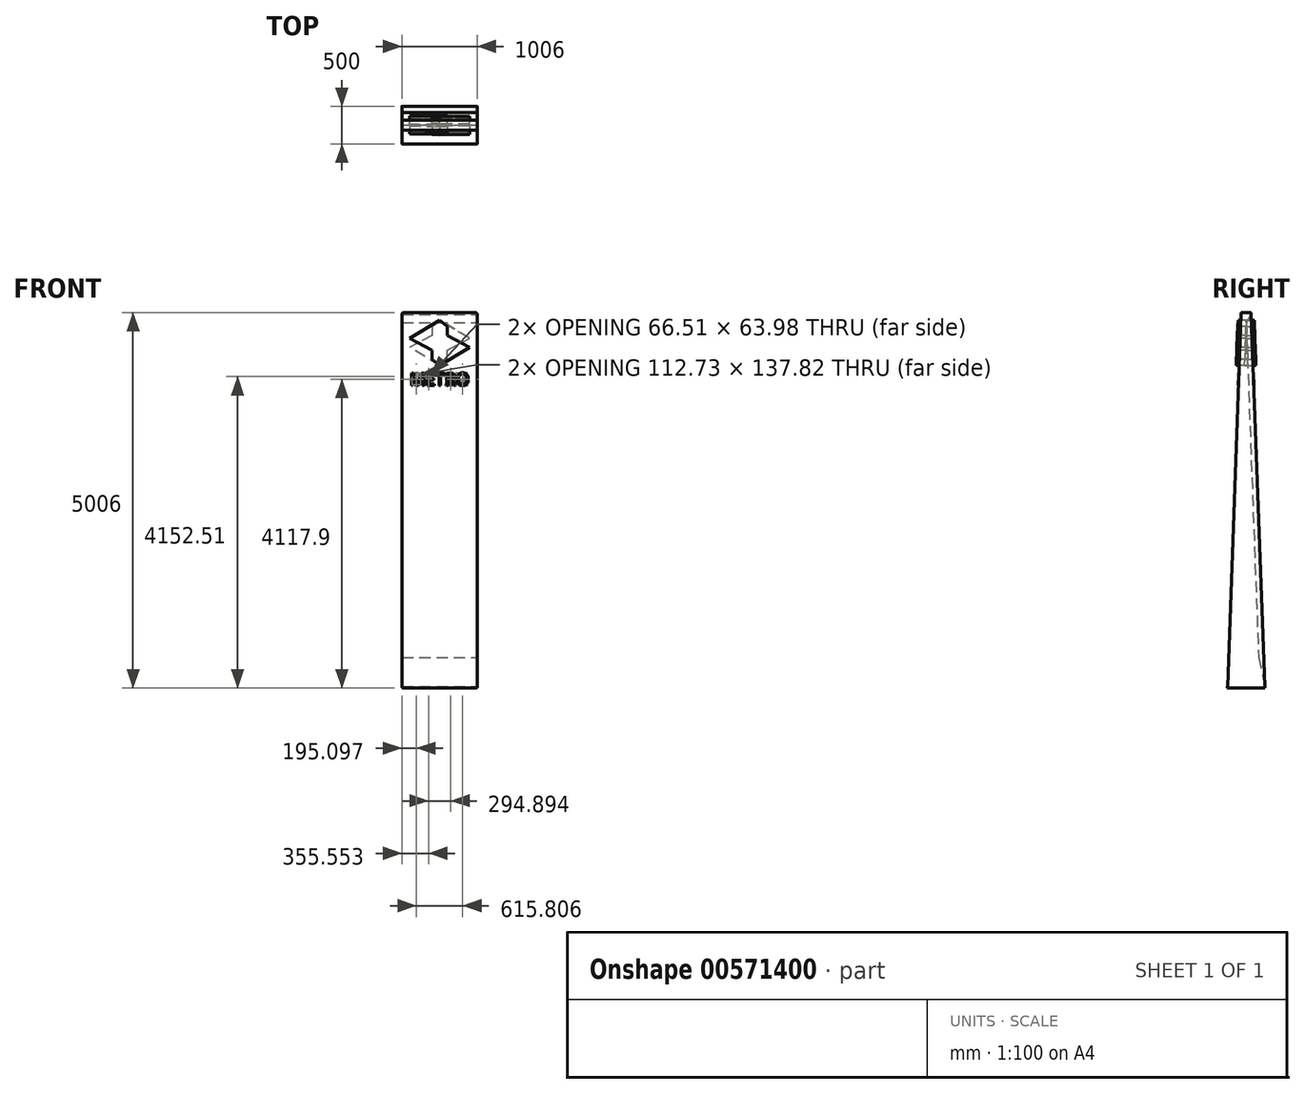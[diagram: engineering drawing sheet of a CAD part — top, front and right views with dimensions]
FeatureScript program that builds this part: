
annotation { "Feature Type Name" : "Feature", "Feature Type Description" : "" }
export const myFeature = defineFeature(function(context is Context, id is Id, definition is map)
    precondition{}
    {
        {
            var Q0;
            Q0=qCreatedBy(makeId("Front.planeOp"),FACE);
            var sketch = newSketch(context, id + "F0", { "sketchPlane" : qUnion([Q0])});
            skLineSegment(sketch, "E0.bottom", {"start": v(-500, 2500) * mm, "end": v(500, 2500) * mm});
            skLineSegment(sketch, "E0.top", {"start": v(-500, -2500) * mm, "end": v(500, -2500) * mm});
            skLineSegment(sketch, "E0.left", {"start": v(-500, 2500) * mm, "end": v(-500, -2500) * mm});
            skLineSegment(sketch, "E0.right", {"start": v(500, 2500) * mm, "end": v(500, -2500) * mm});
            skSolve(sketch);
        }
        {
            var Q0;
            Q0=qSketchRegion(id+"F0",true);
            extrude(context, id + "F1", {"entities" : qUnion([Q0]), "depth" : 500 * mm, "offsetDistance" : 25 * mm, "symmetric" : true});
        }
        {
            var Q0;
            Q0=makeQuery(id+"F1.opExtrude","SWEPT_FACE",FACE,{"disambiguationData":[OSD([sQuery(id+"F0.wireOp",EDGE,"E0.right")])]});
            var sketch = newSketch(context, id + "F2", { "sketchPlane" : qUnion([Q0])});
            skLineSegment(sketch, "E1", {"start": v(0, -2500) * mm, "end": v(0, 2500) * mm, "construction": true});
            skLineSegment(sketch, "E2", {"start": v(-250, -2500) * mm, "end": v(-62.78, 2560) * mm});
            skLineSegment(sketch, "E3", {"start": v(-250, 2500) * mm, "end": v(-250, -2500) * mm});
            skLineSegment(sketch, "E4.MirrorCS", {"start": v(250, 2500) * mm, "end": v(250, -2500) * mm});
            skLineSegment(sketch, "E5.MirrorCS", {"start": v(250, -2500) * mm, "end": v(62.78, 2560) * mm});
            skLineSegment(sketch, "E6", {"start": v(250, 2500) * mm, "end": v(250, 2560) * mm});
            skLineSegment(sketch, "E7", {"start": v(250, 2560) * mm, "end": v(62.78, 2560) * mm});
            skLineSegment(sketch, "E8", {"start": v(-62.78, 2560) * mm, "end": v(-250, 2560) * mm});
            skLineSegment(sketch, "E9", {"start": v(-250, 2560) * mm, "end": v(-250, 2500) * mm});
            skPoint(sketch, "E10", {"position": v(65, 2500) * mm});
            skSolve(sketch);
        }
        {
            var Q0;
            Q0 = qSketchRegion(id + "F2", true);
            extrude(context, id + "F3", {"entities" : qUnion([Q0]), "operationType" : NewBodyOperationType.REMOVE, "endBound" : BoundingType.THROUGH_ALL, "oppositeDirection" : true, "depth" : 25 * mm, "offsetDistance" : 25 * mm});
        }
        {
            var Q0;
            Q0=makeQuery(id+"F1.opExtrude","SWEPT_EDGE",EDGE,{"disambiguationData":[OSD([sQuery(id+"F0.wireOp",EDGE,"E0.bottom"),sQuery(id+"F0.wireOp",EDGE,"E0.left")])]});
            var Q1;
            Q1=makeQuery(id+"F1.opExtrude","SWEPT_EDGE",EDGE,{"disambiguationData":[OSD([sQuery(id+"F0.wireOp",EDGE,"E0.bottom"),sQuery(id+"F0.wireOp",EDGE,"E0.right")])]});
            var Q2;
            Q2=makeQuery(id+"F1.opExtrude","SWEPT_EDGE",EDGE,{"disambiguationData":[OSD([sQuery(id+"F0.wireOp",EDGE,"E0.top"),sQuery(id+"F0.wireOp",EDGE,"E0.left")])]});
            var Q3;
            Q3=makeQuery(id+"F1.opExtrude","SWEPT_EDGE",EDGE,{"disambiguationData":[OSD([sQuery(id+"F0.wireOp",EDGE,"E0.top"),sQuery(id+"F0.wireOp",EDGE,"E0.right")])]});
            fillet(context, id + "F4", {"entities" : qUnion([Q0, Q1, Q2, Q3]), "radius" : 20 * mm, "tangentPropagation" : true, "allowEdgeOverflow" : false});
        }
        {
            var Q0;
            Q0=qCreatedBy(makeId("Front.planeOp"),FACE);
            var sketch = newSketch(context, id + "F5", { "sketchPlane" : qUnion([Q0])});
            skLineSegment(sketch, "E11.0.0", {"start": v(480, -2500) * mm, "end": v(-480, -2500) * mm});
            skArc(sketch, "E11.0.1", {"start": v(-480, -2500) * mm, "mid": v(-494.14, -2494.14) * mm, "end": v(-500, -2480) * mm});
            skLineSegment(sketch, "E11.0.2", {"start": v(-500, -2480) * mm, "end": v(-500, 2480) * mm});
            skArc(sketch, "E11.0.3", {"start": v(-500, 2480) * mm, "mid": v(-494.14, 2494.14) * mm, "end": v(-480, 2500) * mm});
            skLineSegment(sketch, "E11.0.4", {"start": v(-480, 2500) * mm, "end": v(480, 2500) * mm});
            skArc(sketch, "E11.0.5", {"start": v(480, 2500) * mm, "mid": v(494.14, 2494.14) * mm, "end": v(500, 2480) * mm});
            skLineSegment(sketch, "E11.0.6", {"start": v(500, 2480) * mm, "end": v(500, -2480) * mm});
            skArc(sketch, "E11.0.7", {"start": v(500, -2480) * mm, "mid": v(494.14, -2494.14) * mm, "end": v(480, -2500) * mm});
            skArc(sketch, "E12.0", {"start": v(-503, 2480) * mm, "mid": v(-496.26, 2496.26) * mm, "end": v(-480, 2503) * mm});
            skLineSegment(sketch, "E12.1", {"start": v(-503, -2480) * mm, "end": v(-503, 2480) * mm});
            skLineSegment(sketch, "E12.2", {"start": v(-480, 2503) * mm, "end": v(480, 2503) * mm});
            skArc(sketch, "E12.3", {"start": v(-480, -2503) * mm, "mid": v(-496.26, -2496.26) * mm, "end": v(-503, -2480) * mm});
            skArc(sketch, "E12.4", {"start": v(480, 2503) * mm, "mid": v(496.26, 2496.26) * mm, "end": v(503, 2480) * mm});
            skLineSegment(sketch, "E12.5", {"start": v(503, 2480) * mm, "end": v(503, -2480) * mm});
            skArc(sketch, "E12.6", {"start": v(503, -2480) * mm, "mid": v(496.26, -2496.26) * mm, "end": v(480, -2503) * mm});
            skLineSegment(sketch, "E12.7", {"start": v(480, -2503) * mm, "end": v(-480, -2503) * mm});
            skSolve(sketch);
        }
        {
            var Q0;
            Q0=qSketchRegion(id+"F5",true);
            extrude(context, id + "F6", {"entities" : qUnion([Q0]), "depth" : 500 * mm, "offsetDistance" : 25 * mm, "symmetric" : true});
        }
        {
            var Q0;
            Q0=qCreatedBy(makeId("Front.planeOp"),FACE);
            cPlane(context, id + "F7", {"entities" : qUnion([Q0]), "cplaneType" : CPlaneType.OFFSET, "offset" : 730 * mm, "width" : 150 * mm, "height" : 150 * mm});
        }
        {
            var Q0;
            Q0 = qSketchRegion(id + "F2", true);
            extrude(context, id + "F8", {"entities" : qUnion([Q0]), "operationType" : NewBodyOperationType.REMOVE, "oppositeDirection" : true, "depth" : 5000 * mm, "offsetDistance" : 25 * mm, "symmetric" : true});
        }
        {
            var Q0;
            Q0=qCreatedBy(id+"F7.planeOp",FACE);
            var sketch = newSketch(context, id + "F9", { "sketchPlane" : qUnion([Q0])});
            skLineSegment(sketch, "E13", {"start": v(0, 0) * mm, "end": v(0, 2768.76) * mm, "construction": true});
            skLineSegment(sketch, "E14.0", {"start": v(-479.83, 2500) * mm, "end": v(480, 2500) * mm, "construction": true});
            skLineSegment(sketch, "E15", {"start": v(-400, 2100) * mm, "end": v(400, 2100) * mm, "construction": true});
            skLineSegment(sketch, "E16", {"start": v(-400, 2400) * mm, "end": v(-400, 1800) * mm, "construction": true});
            skLineSegment(sketch, "E17", {"start": v(-400, 2400) * mm, "end": v(400, 2400) * mm, "construction": true});
            skLineSegment(sketch, "E18", {"start": v(400, 2400) * mm, "end": v(400, 1800) * mm, "construction": true});
            skLineSegment(sketch, "E19", {"start": v(400, 1800) * mm, "end": v(-400, 1800) * mm, "construction": true});
            skLineSegment(sketch, "E20", {"start": v(-120, 1800) * mm, "end": v(-120, 2400) * mm, "construction": true});
            skLineSegment(sketch, "E21", {"start": v(120, 2400) * mm, "end": v(120, 1800) * mm, "construction": true});
            skLineSegment(sketch, "E22", {"start": v(-400, 2160) * mm, "end": v(400, 2160) * mm, "construction": true});
            skLineSegment(sketch, "E23", {"start": v(-400, 2040) * mm, "end": v(400, 2040) * mm, "construction": true});
            skPoint(sketch, "E24", {"position": v(0, 2400) * mm});
            skLineSegment(sketch, "E25", {"start": v(100, 2320) * mm, "end": v(100, 2200) * mm});
            skLineSegment(sketch, "E26", {"start": v(100, 2200) * mm, "end": v(400, 2040) * mm});
            skLineSegment(sketch, "E27", {"start": v(-100, 1880) * mm, "end": v(-100, 2000) * mm});
            skLineSegment(sketch, "E28", {"start": v(-100, 2000) * mm, "end": v(-400, 2160) * mm});
            skLineSegment(sketch, "E29", {"start": v(-100, 1880) * mm, "end": v(0, 1800) * mm});
            skLineSegment(sketch, "E30", {"start": v(0, 1800) * mm, "end": v(400, 2040) * mm});
            skLineSegment(sketch, "E31", {"start": v(100, 2320) * mm, "end": v(0, 2400) * mm});
            skLineSegment(sketch, "E32", {"start": v(-400, 2160) * mm, "end": v(0, 2400) * mm});
            skSolve(sketch);
        }
        {
            var Q0;
            Q0=qSketchRegion(id+"F9",true);
            extrude(context, id + "F10", {"entities" : qUnion([Q0]), "oppositeDirection" : true, "depth" : 800 * mm, "offsetDistance" : 25 * mm});
        }
        {
            var Q0;
            Q0=makeQuery(id+"F1.opExtrude","SWEPT_FACE",FACE,{"disambiguationData":[OSD([sQuery(id+"F0.wireOp",EDGE,"E0.right")])]});
            var sketch = newSketch(context, id + "F11", { "sketchPlane" : qUnion([Q0])});
            skLineSegment(sketch, "E33.0", {"start": v(-289.57, -2487.76) * mm, "end": v(-106.05, 2472.24) * mm});
            skLineSegment(sketch, "E34", {"start": v(-106.05, 2472.24) * mm, "end": v(-840.5, 2445.07) * mm});
            skLineSegment(sketch, "E35", {"start": v(-840.5, 2445.07) * mm, "end": v(-289.57, -2487.76) * mm});
            skLineSegment(sketch, "E36", {"start": v(65.74, 2480) * mm, "end": v(918.94, 2448.43) * mm});
            skLineSegment(sketch, "E37", {"start": v(918.94, 2448.43) * mm, "end": v(249.26, -2480) * mm});
            skLineSegment(sketch, "E38", {"start": v(65.74, 2480) * mm, "end": v(0, 2371.47) * mm});
            skPoint(sketch, "E38.endSnap0", {"position": v(0, 2480) * mm});
            skLineSegment(sketch, "E39", {"start": v(0, 2371.47) * mm, "end": v(165.33, -2096.89) * mm});
            skLineSegment(sketch, "E40", {"start": v(165.33, -2096.89) * mm, "end": v(249.26, -2480) * mm});
            skSolve(sketch);
        }
        {
            var Q0;
            Q0 = qSketchRegion(id + "F11", true);
            extrude(context, id + "F12", {"entities" : qUnion([Q0]), "operationType" : NewBodyOperationType.REMOVE, "endBound" : BoundingType.THROUGH_ALL, "oppositeDirection" : true, "depth" : 25 * mm, "offsetDistance" : 25 * mm});
        }
        {
            var Q0;
            Q0=qCreatedBy(id+"F7.planeOp",FACE);
            var sketch = newSketch(context, id + "F13", { "sketchPlane" : qUnion([Q0])});
            skText(sketch, "E41", { "text": "METRO", "fontName": "OpenSans-Regular.ttf"});
            const initialGuessF13  = {"E41": [-0.39992, 1.53123, 1, 0, 0.16877]};
            skSetInitialGuess(sketch, initialGuessF13);
            skSolve(sketch);
        }
        {
            var Q0;
            Q0=qSketchRegion(id+"F13",true);
            var Q1;
            Q1=makeQuery(id+"F3.boolean.opBoolean","COPY",FACE,{"derivedFrom":makeQuery(id+"F3.opExtrude","SWEPT_FACE",FACE,{"disambiguationData":[OSD([sQuery(id+"F2.wireOp",EDGE,"E2")])]})});
            extrude(context, id + "F14", {"entities" : qUnion([Q0]), "endBound" : BoundingType.UP_TO_SURFACE, "oppositeDirection" : true, "depth" : 25 * mm, "endBoundEntityFace" : qUnion([Q1]), "offsetDistance" : 25 * mm});
        }
        {
            var Q0;
            Q0=makeQuery(id+"F1.opExtrude","SWEPT_FACE",FACE,{"disambiguationData":[OSD([sQuery(id+"F0.wireOp",EDGE,"E0.right")])]});
            var sketch = newSketch(context, id + "F15", { "sketchPlane" : qUnion([Q0])});
            skLineSegment(sketch, "E42.0", {"start": v(-109.8, 1424.3) * mm, "end": v(-98.9, 1718.76) * mm});
            skLineSegment(sketch, "E43", {"start": v(-98.9, 1718.76) * mm, "end": v(-869.9, 1736.78) * mm});
            skLineSegment(sketch, "E44", {"start": v(-869.9, 1736.78) * mm, "end": v(-869.9, 1424.3) * mm});
            skLineSegment(sketch, "E45", {"start": v(-869.9, 1424.3) * mm, "end": v(-109.8, 1424.3) * mm});
            skSolve(sketch);
        }
        {
            var Q0;
            Q0=qSketchRegion(id+"F15",true);
            extrude(context, id + "F16", {"entities" : qUnion([Q0]), "operationType" : NewBodyOperationType.REMOVE, "endBound" : BoundingType.THROUGH_ALL, "oppositeDirection" : true, "depth" : 25 * mm, "offsetDistance" : 25 * mm});
        }
        {
            var Q0;
            Q0=makeQuery(id+"F10.opExtrude","SWEPT_BODY",BODY,{"disambiguationData":[OSD([sQuery(id+"F9.wireOp",EDGE,"E25"),sQuery(id+"F9.wireOp",EDGE,"E26"),sQuery(id+"F9.wireOp",EDGE,"E27"),sQuery(id+"F9.wireOp",EDGE,"E28"),sQuery(id+"F9.wireOp",EDGE,"E29"),sQuery(id+"F9.wireOp",EDGE,"E30"),sQuery(id+"F9.wireOp",EDGE,"E31"),sQuery(id+"F9.wireOp",EDGE,"E32")])]});
            var Q1;
            Q1=makeQuery(id+"F14.opExtrude","SWEPT_BODY",BODY,{"disambiguationData":[OSD([sQuery(id+"F13.wireOp",EDGE,"E41.sketch_text.stroke-56"),sQuery(id+"F13.wireOp",EDGE,"E41.sketch_text.stroke-57"),sQuery(id+"F13.wireOp",EDGE,"E41.sketch_text.stroke-58"),sQuery(id+"F13.wireOp",EDGE,"E41.sketch_text.stroke-59"),sQuery(id+"F13.wireOp",EDGE,"E41.sketch_text.stroke-60"),sQuery(id+"F13.wireOp",EDGE,"E41.sketch_text.stroke-61"),sQuery(id+"F13.wireOp",EDGE,"E41.sketch_text.stroke-62"),sQuery(id+"F13.wireOp",EDGE,"E41.sketch_text.stroke-63"),sQuery(id+"F13.wireOp",EDGE,"E41.sketch_text.stroke-64"),sQuery(id+"F13.wireOp",EDGE,"E41.sketch_text.stroke-65"),sQuery(id+"F13.wireOp",EDGE,"E41.sketch_text.stroke-66"),sQuery(id+"F13.wireOp",EDGE,"E41.sketch_text.stroke-67"),sQuery(id+"F13.wireOp",EDGE,"E41.sketch_text.stroke-68"),sQuery(id+"F13.wireOp",EDGE,"E41.sketch_text.stroke-69"),sQuery(id+"F13.wireOp",EDGE,"E41.sketch_text.stroke-70"),sQuery(id+"F13.wireOp",EDGE,"E41.sketch_text.stroke-71")])]});
            var Q2;
            Q2=makeQuery(id+"F14.opExtrude","SWEPT_BODY",BODY,{"disambiguationData":[OSD([sQuery(id+"F13.wireOp",EDGE,"E41.sketch_text.stroke-38"),sQuery(id+"F13.wireOp",EDGE,"E41.sketch_text.stroke-39"),sQuery(id+"F13.wireOp",EDGE,"E41.sketch_text.stroke-40"),sQuery(id+"F13.wireOp",EDGE,"E41.sketch_text.stroke-41"),sQuery(id+"F13.wireOp",EDGE,"E41.sketch_text.stroke-42"),sQuery(id+"F13.wireOp",EDGE,"E41.sketch_text.stroke-43"),sQuery(id+"F13.wireOp",EDGE,"E41.sketch_text.stroke-44"),sQuery(id+"F13.wireOp",EDGE,"E41.sketch_text.stroke-45"),sQuery(id+"F13.wireOp",EDGE,"E41.sketch_text.stroke-46"),sQuery(id+"F13.wireOp",EDGE,"E41.sketch_text.stroke-47"),sQuery(id+"F13.wireOp",EDGE,"E41.sketch_text.stroke-48"),sQuery(id+"F13.wireOp",EDGE,"E41.sketch_text.stroke-49"),sQuery(id+"F13.wireOp",EDGE,"E41.sketch_text.stroke-50"),sQuery(id+"F13.wireOp",EDGE,"E41.sketch_text.stroke-51"),sQuery(id+"F13.wireOp",EDGE,"E41.sketch_text.stroke-52"),sQuery(id+"F13.wireOp",EDGE,"E41.sketch_text.stroke-53"),sQuery(id+"F13.wireOp",EDGE,"E41.sketch_text.stroke-54"),sQuery(id+"F13.wireOp",EDGE,"E41.sketch_text.stroke-55")])]});
            var Q3;
            Q3=makeQuery(id+"F14.opExtrude","SWEPT_BODY",BODY,{"disambiguationData":[OSD([sQuery(id+"F13.wireOp",EDGE,"E41.sketch_text.stroke-30"),sQuery(id+"F13.wireOp",EDGE,"E41.sketch_text.stroke-31"),sQuery(id+"F13.wireOp",EDGE,"E41.sketch_text.stroke-32"),sQuery(id+"F13.wireOp",EDGE,"E41.sketch_text.stroke-33"),sQuery(id+"F13.wireOp",EDGE,"E41.sketch_text.stroke-34"),sQuery(id+"F13.wireOp",EDGE,"E41.sketch_text.stroke-35"),sQuery(id+"F13.wireOp",EDGE,"E41.sketch_text.stroke-36"),sQuery(id+"F13.wireOp",EDGE,"E41.sketch_text.stroke-37")])]});
            var Q4;
            Q4=makeQuery(id+"F14.opExtrude","SWEPT_BODY",BODY,{"disambiguationData":[OSD([sQuery(id+"F13.wireOp",EDGE,"E41.sketch_text.stroke-18"),sQuery(id+"F13.wireOp",EDGE,"E41.sketch_text.stroke-19"),sQuery(id+"F13.wireOp",EDGE,"E41.sketch_text.stroke-20"),sQuery(id+"F13.wireOp",EDGE,"E41.sketch_text.stroke-21"),sQuery(id+"F13.wireOp",EDGE,"E41.sketch_text.stroke-22"),sQuery(id+"F13.wireOp",EDGE,"E41.sketch_text.stroke-23"),sQuery(id+"F13.wireOp",EDGE,"E41.sketch_text.stroke-24"),sQuery(id+"F13.wireOp",EDGE,"E41.sketch_text.stroke-25"),sQuery(id+"F13.wireOp",EDGE,"E41.sketch_text.stroke-26"),sQuery(id+"F13.wireOp",EDGE,"E41.sketch_text.stroke-27"),sQuery(id+"F13.wireOp",EDGE,"E41.sketch_text.stroke-28"),sQuery(id+"F13.wireOp",EDGE,"E41.sketch_text.stroke-29")])]});
            var Q5;
            Q5=makeQuery(id+"F14.opExtrude","SWEPT_BODY",BODY,{"disambiguationData":[OSD([sQuery(id+"F13.wireOp",EDGE,"E41.sketch_text.stroke-0"),sQuery(id+"F13.wireOp",EDGE,"E41.sketch_text.stroke-1"),sQuery(id+"F13.wireOp",EDGE,"E41.sketch_text.stroke-2"),sQuery(id+"F13.wireOp",EDGE,"E41.sketch_text.stroke-3"),sQuery(id+"F13.wireOp",EDGE,"E41.sketch_text.stroke-4"),sQuery(id+"F13.wireOp",EDGE,"E41.sketch_text.stroke-5"),sQuery(id+"F13.wireOp",EDGE,"E41.sketch_text.stroke-6"),sQuery(id+"F13.wireOp",EDGE,"E41.sketch_text.stroke-7"),sQuery(id+"F13.wireOp",EDGE,"E41.sketch_text.stroke-8"),sQuery(id+"F13.wireOp",EDGE,"E41.sketch_text.stroke-9"),sQuery(id+"F13.wireOp",EDGE,"E41.sketch_text.stroke-10"),sQuery(id+"F13.wireOp",EDGE,"E41.sketch_text.stroke-11"),sQuery(id+"F13.wireOp",EDGE,"E41.sketch_text.stroke-12"),sQuery(id+"F13.wireOp",EDGE,"E41.sketch_text.stroke-13"),sQuery(id+"F13.wireOp",EDGE,"E41.sketch_text.stroke-14"),sQuery(id+"F13.wireOp",EDGE,"E41.sketch_text.stroke-15"),sQuery(id+"F13.wireOp",EDGE,"E41.sketch_text.stroke-16"),sQuery(id+"F13.wireOp",EDGE,"E41.sketch_text.stroke-17")])]});
            var Q6;
            Q6=qCreatedBy(makeId("Front.planeOp"),FACE);
            mirror(context, id + "F17", {"entities" : qUnion([Q0, Q1, Q2, Q3, Q4, Q5]), "mirrorPlane" : qUnion([Q6])});
        }
        {
            var Q0;
            Q0=makeQuery(id+"F17.opPattern","COPY",BODY,{"derivedFrom":makeQuery(id+"F10.opExtrude","SWEPT_BODY",BODY,{"disambiguationData":[OSD([sQuery(id+"F9.wireOp",EDGE,"E25"),sQuery(id+"F9.wireOp",EDGE,"E26"),sQuery(id+"F9.wireOp",EDGE,"E27"),sQuery(id+"F9.wireOp",EDGE,"E28"),sQuery(id+"F9.wireOp",EDGE,"E29"),sQuery(id+"F9.wireOp",EDGE,"E30"),sQuery(id+"F9.wireOp",EDGE,"E31"),sQuery(id+"F9.wireOp",EDGE,"E32")])]}),"instanceName":"1"});
            var Q1;
            Q1=makeQuery(id+"F17.opPattern","COPY",BODY,{"derivedFrom":makeQuery(id+"F14.opExtrude","SWEPT_BODY",BODY,{"disambiguationData":[OSD([sQuery(id+"F13.wireOp",EDGE,"E41.sketch_text.stroke-56"),sQuery(id+"F13.wireOp",EDGE,"E41.sketch_text.stroke-57"),sQuery(id+"F13.wireOp",EDGE,"E41.sketch_text.stroke-58"),sQuery(id+"F13.wireOp",EDGE,"E41.sketch_text.stroke-59"),sQuery(id+"F13.wireOp",EDGE,"E41.sketch_text.stroke-60"),sQuery(id+"F13.wireOp",EDGE,"E41.sketch_text.stroke-61"),sQuery(id+"F13.wireOp",EDGE,"E41.sketch_text.stroke-62"),sQuery(id+"F13.wireOp",EDGE,"E41.sketch_text.stroke-63"),sQuery(id+"F13.wireOp",EDGE,"E41.sketch_text.stroke-64"),sQuery(id+"F13.wireOp",EDGE,"E41.sketch_text.stroke-65"),sQuery(id+"F13.wireOp",EDGE,"E41.sketch_text.stroke-66"),sQuery(id+"F13.wireOp",EDGE,"E41.sketch_text.stroke-67"),sQuery(id+"F13.wireOp",EDGE,"E41.sketch_text.stroke-68"),sQuery(id+"F13.wireOp",EDGE,"E41.sketch_text.stroke-69"),sQuery(id+"F13.wireOp",EDGE,"E41.sketch_text.stroke-70"),sQuery(id+"F13.wireOp",EDGE,"E41.sketch_text.stroke-71")])]}),"instanceName":"1"});
            var Q2;
            Q2=makeQuery(id+"F17.opPattern","COPY",BODY,{"derivedFrom":makeQuery(id+"F14.opExtrude","SWEPT_BODY",BODY,{"disambiguationData":[OSD([sQuery(id+"F13.wireOp",EDGE,"E41.sketch_text.stroke-38"),sQuery(id+"F13.wireOp",EDGE,"E41.sketch_text.stroke-39"),sQuery(id+"F13.wireOp",EDGE,"E41.sketch_text.stroke-40"),sQuery(id+"F13.wireOp",EDGE,"E41.sketch_text.stroke-41"),sQuery(id+"F13.wireOp",EDGE,"E41.sketch_text.stroke-42"),sQuery(id+"F13.wireOp",EDGE,"E41.sketch_text.stroke-43"),sQuery(id+"F13.wireOp",EDGE,"E41.sketch_text.stroke-44"),sQuery(id+"F13.wireOp",EDGE,"E41.sketch_text.stroke-45"),sQuery(id+"F13.wireOp",EDGE,"E41.sketch_text.stroke-46"),sQuery(id+"F13.wireOp",EDGE,"E41.sketch_text.stroke-47"),sQuery(id+"F13.wireOp",EDGE,"E41.sketch_text.stroke-48"),sQuery(id+"F13.wireOp",EDGE,"E41.sketch_text.stroke-49"),sQuery(id+"F13.wireOp",EDGE,"E41.sketch_text.stroke-50"),sQuery(id+"F13.wireOp",EDGE,"E41.sketch_text.stroke-51"),sQuery(id+"F13.wireOp",EDGE,"E41.sketch_text.stroke-52"),sQuery(id+"F13.wireOp",EDGE,"E41.sketch_text.stroke-53"),sQuery(id+"F13.wireOp",EDGE,"E41.sketch_text.stroke-54"),sQuery(id+"F13.wireOp",EDGE,"E41.sketch_text.stroke-55")])]}),"instanceName":"1"});
            var Q3;
            Q3=makeQuery(id+"F17.opPattern","COPY",BODY,{"derivedFrom":makeQuery(id+"F14.opExtrude","SWEPT_BODY",BODY,{"disambiguationData":[OSD([sQuery(id+"F13.wireOp",EDGE,"E41.sketch_text.stroke-30"),sQuery(id+"F13.wireOp",EDGE,"E41.sketch_text.stroke-31"),sQuery(id+"F13.wireOp",EDGE,"E41.sketch_text.stroke-32"),sQuery(id+"F13.wireOp",EDGE,"E41.sketch_text.stroke-33"),sQuery(id+"F13.wireOp",EDGE,"E41.sketch_text.stroke-34"),sQuery(id+"F13.wireOp",EDGE,"E41.sketch_text.stroke-35"),sQuery(id+"F13.wireOp",EDGE,"E41.sketch_text.stroke-36"),sQuery(id+"F13.wireOp",EDGE,"E41.sketch_text.stroke-37")])]}),"instanceName":"1"});
            var Q4;
            Q4=makeQuery(id+"F17.opPattern","COPY",BODY,{"derivedFrom":makeQuery(id+"F14.opExtrude","SWEPT_BODY",BODY,{"disambiguationData":[OSD([sQuery(id+"F13.wireOp",EDGE,"E41.sketch_text.stroke-18"),sQuery(id+"F13.wireOp",EDGE,"E41.sketch_text.stroke-19"),sQuery(id+"F13.wireOp",EDGE,"E41.sketch_text.stroke-20"),sQuery(id+"F13.wireOp",EDGE,"E41.sketch_text.stroke-21"),sQuery(id+"F13.wireOp",EDGE,"E41.sketch_text.stroke-22"),sQuery(id+"F13.wireOp",EDGE,"E41.sketch_text.stroke-23"),sQuery(id+"F13.wireOp",EDGE,"E41.sketch_text.stroke-24"),sQuery(id+"F13.wireOp",EDGE,"E41.sketch_text.stroke-25"),sQuery(id+"F13.wireOp",EDGE,"E41.sketch_text.stroke-26"),sQuery(id+"F13.wireOp",EDGE,"E41.sketch_text.stroke-27"),sQuery(id+"F13.wireOp",EDGE,"E41.sketch_text.stroke-28"),sQuery(id+"F13.wireOp",EDGE,"E41.sketch_text.stroke-29")])]}),"instanceName":"1"});
            var Q5;
            Q5=makeQuery(id+"F17.opPattern","COPY",BODY,{"derivedFrom":makeQuery(id+"F14.opExtrude","SWEPT_BODY",BODY,{"disambiguationData":[OSD([sQuery(id+"F13.wireOp",EDGE,"E41.sketch_text.stroke-0"),sQuery(id+"F13.wireOp",EDGE,"E41.sketch_text.stroke-1"),sQuery(id+"F13.wireOp",EDGE,"E41.sketch_text.stroke-2"),sQuery(id+"F13.wireOp",EDGE,"E41.sketch_text.stroke-3"),sQuery(id+"F13.wireOp",EDGE,"E41.sketch_text.stroke-4"),sQuery(id+"F13.wireOp",EDGE,"E41.sketch_text.stroke-5"),sQuery(id+"F13.wireOp",EDGE,"E41.sketch_text.stroke-6"),sQuery(id+"F13.wireOp",EDGE,"E41.sketch_text.stroke-7"),sQuery(id+"F13.wireOp",EDGE,"E41.sketch_text.stroke-8"),sQuery(id+"F13.wireOp",EDGE,"E41.sketch_text.stroke-9"),sQuery(id+"F13.wireOp",EDGE,"E41.sketch_text.stroke-10"),sQuery(id+"F13.wireOp",EDGE,"E41.sketch_text.stroke-11"),sQuery(id+"F13.wireOp",EDGE,"E41.sketch_text.stroke-12"),sQuery(id+"F13.wireOp",EDGE,"E41.sketch_text.stroke-13"),sQuery(id+"F13.wireOp",EDGE,"E41.sketch_text.stroke-14"),sQuery(id+"F13.wireOp",EDGE,"E41.sketch_text.stroke-15"),sQuery(id+"F13.wireOp",EDGE,"E41.sketch_text.stroke-16"),sQuery(id+"F13.wireOp",EDGE,"E41.sketch_text.stroke-17")])]}),"instanceName":"1"});
            var Q6;
            Q6=qCreatedBy(makeId("Right.planeOp"),FACE);
            mirror(context, id + "F18", {"entities" : qUnion([Q0, Q1, Q2, Q3, Q4, Q5]), "mirrorPlane" : qUnion([Q6])});
        }
        {
            var Q0;
            Q0=makeQuery(id+"F17.opPattern","COPY",BODY,{"derivedFrom":makeQuery(id+"F10.opExtrude","SWEPT_BODY",BODY,{"disambiguationData":[OSD([sQuery(id+"F9.wireOp",EDGE,"E25"),sQuery(id+"F9.wireOp",EDGE,"E26"),sQuery(id+"F9.wireOp",EDGE,"E27"),sQuery(id+"F9.wireOp",EDGE,"E28"),sQuery(id+"F9.wireOp",EDGE,"E29"),sQuery(id+"F9.wireOp",EDGE,"E30"),sQuery(id+"F9.wireOp",EDGE,"E31"),sQuery(id+"F9.wireOp",EDGE,"E32")])]}),"instanceName":"1"});
            var Q1;
            Q1=makeQuery(id+"F17.opPattern","COPY",BODY,{"derivedFrom":makeQuery(id+"F14.opExtrude","SWEPT_BODY",BODY,{"disambiguationData":[OSD([sQuery(id+"F13.wireOp",EDGE,"E41.sketch_text.stroke-0"),sQuery(id+"F13.wireOp",EDGE,"E41.sketch_text.stroke-1"),sQuery(id+"F13.wireOp",EDGE,"E41.sketch_text.stroke-2"),sQuery(id+"F13.wireOp",EDGE,"E41.sketch_text.stroke-3"),sQuery(id+"F13.wireOp",EDGE,"E41.sketch_text.stroke-4"),sQuery(id+"F13.wireOp",EDGE,"E41.sketch_text.stroke-5"),sQuery(id+"F13.wireOp",EDGE,"E41.sketch_text.stroke-6"),sQuery(id+"F13.wireOp",EDGE,"E41.sketch_text.stroke-7"),sQuery(id+"F13.wireOp",EDGE,"E41.sketch_text.stroke-8"),sQuery(id+"F13.wireOp",EDGE,"E41.sketch_text.stroke-9"),sQuery(id+"F13.wireOp",EDGE,"E41.sketch_text.stroke-10"),sQuery(id+"F13.wireOp",EDGE,"E41.sketch_text.stroke-11"),sQuery(id+"F13.wireOp",EDGE,"E41.sketch_text.stroke-12"),sQuery(id+"F13.wireOp",EDGE,"E41.sketch_text.stroke-13"),sQuery(id+"F13.wireOp",EDGE,"E41.sketch_text.stroke-14"),sQuery(id+"F13.wireOp",EDGE,"E41.sketch_text.stroke-15"),sQuery(id+"F13.wireOp",EDGE,"E41.sketch_text.stroke-16"),sQuery(id+"F13.wireOp",EDGE,"E41.sketch_text.stroke-17")])]}),"instanceName":"1"});
            var Q2;
            Q2=makeQuery(id+"F17.opPattern","COPY",BODY,{"derivedFrom":makeQuery(id+"F14.opExtrude","SWEPT_BODY",BODY,{"disambiguationData":[OSD([sQuery(id+"F13.wireOp",EDGE,"E41.sketch_text.stroke-18"),sQuery(id+"F13.wireOp",EDGE,"E41.sketch_text.stroke-19"),sQuery(id+"F13.wireOp",EDGE,"E41.sketch_text.stroke-20"),sQuery(id+"F13.wireOp",EDGE,"E41.sketch_text.stroke-21"),sQuery(id+"F13.wireOp",EDGE,"E41.sketch_text.stroke-22"),sQuery(id+"F13.wireOp",EDGE,"E41.sketch_text.stroke-23"),sQuery(id+"F13.wireOp",EDGE,"E41.sketch_text.stroke-24"),sQuery(id+"F13.wireOp",EDGE,"E41.sketch_text.stroke-25"),sQuery(id+"F13.wireOp",EDGE,"E41.sketch_text.stroke-26"),sQuery(id+"F13.wireOp",EDGE,"E41.sketch_text.stroke-27"),sQuery(id+"F13.wireOp",EDGE,"E41.sketch_text.stroke-28"),sQuery(id+"F13.wireOp",EDGE,"E41.sketch_text.stroke-29")])]}),"instanceName":"1"});
            var Q3;
            Q3=makeQuery(id+"F17.opPattern","COPY",BODY,{"derivedFrom":makeQuery(id+"F14.opExtrude","SWEPT_BODY",BODY,{"disambiguationData":[OSD([sQuery(id+"F13.wireOp",EDGE,"E41.sketch_text.stroke-38"),sQuery(id+"F13.wireOp",EDGE,"E41.sketch_text.stroke-39"),sQuery(id+"F13.wireOp",EDGE,"E41.sketch_text.stroke-40"),sQuery(id+"F13.wireOp",EDGE,"E41.sketch_text.stroke-41"),sQuery(id+"F13.wireOp",EDGE,"E41.sketch_text.stroke-42"),sQuery(id+"F13.wireOp",EDGE,"E41.sketch_text.stroke-43"),sQuery(id+"F13.wireOp",EDGE,"E41.sketch_text.stroke-44"),sQuery(id+"F13.wireOp",EDGE,"E41.sketch_text.stroke-45"),sQuery(id+"F13.wireOp",EDGE,"E41.sketch_text.stroke-46"),sQuery(id+"F13.wireOp",EDGE,"E41.sketch_text.stroke-47"),sQuery(id+"F13.wireOp",EDGE,"E41.sketch_text.stroke-48"),sQuery(id+"F13.wireOp",EDGE,"E41.sketch_text.stroke-49"),sQuery(id+"F13.wireOp",EDGE,"E41.sketch_text.stroke-50"),sQuery(id+"F13.wireOp",EDGE,"E41.sketch_text.stroke-51"),sQuery(id+"F13.wireOp",EDGE,"E41.sketch_text.stroke-52"),sQuery(id+"F13.wireOp",EDGE,"E41.sketch_text.stroke-53"),sQuery(id+"F13.wireOp",EDGE,"E41.sketch_text.stroke-54"),sQuery(id+"F13.wireOp",EDGE,"E41.sketch_text.stroke-55")])]}),"instanceName":"1"});
            var Q4;
            Q4=makeQuery(id+"F17.opPattern","COPY",BODY,{"derivedFrom":makeQuery(id+"F14.opExtrude","SWEPT_BODY",BODY,{"disambiguationData":[OSD([sQuery(id+"F13.wireOp",EDGE,"E41.sketch_text.stroke-56"),sQuery(id+"F13.wireOp",EDGE,"E41.sketch_text.stroke-57"),sQuery(id+"F13.wireOp",EDGE,"E41.sketch_text.stroke-58"),sQuery(id+"F13.wireOp",EDGE,"E41.sketch_text.stroke-59"),sQuery(id+"F13.wireOp",EDGE,"E41.sketch_text.stroke-60"),sQuery(id+"F13.wireOp",EDGE,"E41.sketch_text.stroke-61"),sQuery(id+"F13.wireOp",EDGE,"E41.sketch_text.stroke-62"),sQuery(id+"F13.wireOp",EDGE,"E41.sketch_text.stroke-63"),sQuery(id+"F13.wireOp",EDGE,"E41.sketch_text.stroke-64"),sQuery(id+"F13.wireOp",EDGE,"E41.sketch_text.stroke-65"),sQuery(id+"F13.wireOp",EDGE,"E41.sketch_text.stroke-66"),sQuery(id+"F13.wireOp",EDGE,"E41.sketch_text.stroke-67"),sQuery(id+"F13.wireOp",EDGE,"E41.sketch_text.stroke-68"),sQuery(id+"F13.wireOp",EDGE,"E41.sketch_text.stroke-69"),sQuery(id+"F13.wireOp",EDGE,"E41.sketch_text.stroke-70"),sQuery(id+"F13.wireOp",EDGE,"E41.sketch_text.stroke-71")])]}),"instanceName":"1"});
            var Q5;
            Q5=makeQuery(id+"F17.opPattern","COPY",BODY,{"derivedFrom":makeQuery(id+"F14.opExtrude","SWEPT_BODY",BODY,{"disambiguationData":[OSD([sQuery(id+"F13.wireOp",EDGE,"E41.sketch_text.stroke-30"),sQuery(id+"F13.wireOp",EDGE,"E41.sketch_text.stroke-31"),sQuery(id+"F13.wireOp",EDGE,"E41.sketch_text.stroke-32"),sQuery(id+"F13.wireOp",EDGE,"E41.sketch_text.stroke-33"),sQuery(id+"F13.wireOp",EDGE,"E41.sketch_text.stroke-34"),sQuery(id+"F13.wireOp",EDGE,"E41.sketch_text.stroke-35"),sQuery(id+"F13.wireOp",EDGE,"E41.sketch_text.stroke-36"),sQuery(id+"F13.wireOp",EDGE,"E41.sketch_text.stroke-37")])]}),"instanceName":"1"});
            deleteBodies(context, id + "F19", {"entities" : qUnion([Q0, Q1, Q2, Q3, Q4, Q5])});
        }
    });
